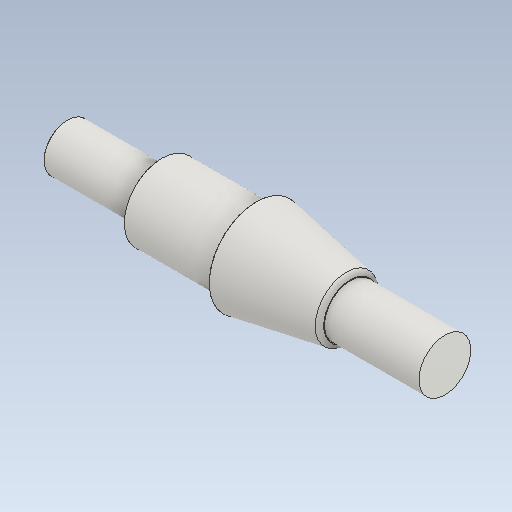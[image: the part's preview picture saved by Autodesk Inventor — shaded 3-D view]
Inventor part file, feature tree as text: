
AUTODESK INVENTOR PART (.ipt)
format: ipt  version: 2021 (Build 250183000, 183)  size: 141,824 bytes
history: native  units: mm
features: chamfer x3, other x3, fillet x2, revolve x1
ambient origin geometry x6: Origin, XZ Plane, XY Plane, X Axis, Y Axis, Z Axis
bodies: Solid1 (feature_tree)
feature tree (9):
  revolve  "Revolution1"  [1 undecoded]
  chamfer  "Chamfer1"  Distance=50.0mm
  fillet  "Fillet1"  Radius=80.0mm
  chamfer  "Chamfer2"  Distance=55.0mm
  chamfer  "Chamfer3"  [1 undecoded]
  fillet  "Fillet2"  Radius=0.5mm
  other  "Start Plane"
  other  "Origin point"
  other  "Main Sketch"
note: 2 required parameter values undecoded (feature->parameter linkage not recoverable at this tier; creation-order binding heuristic only, values carry confidence <= 0.55)